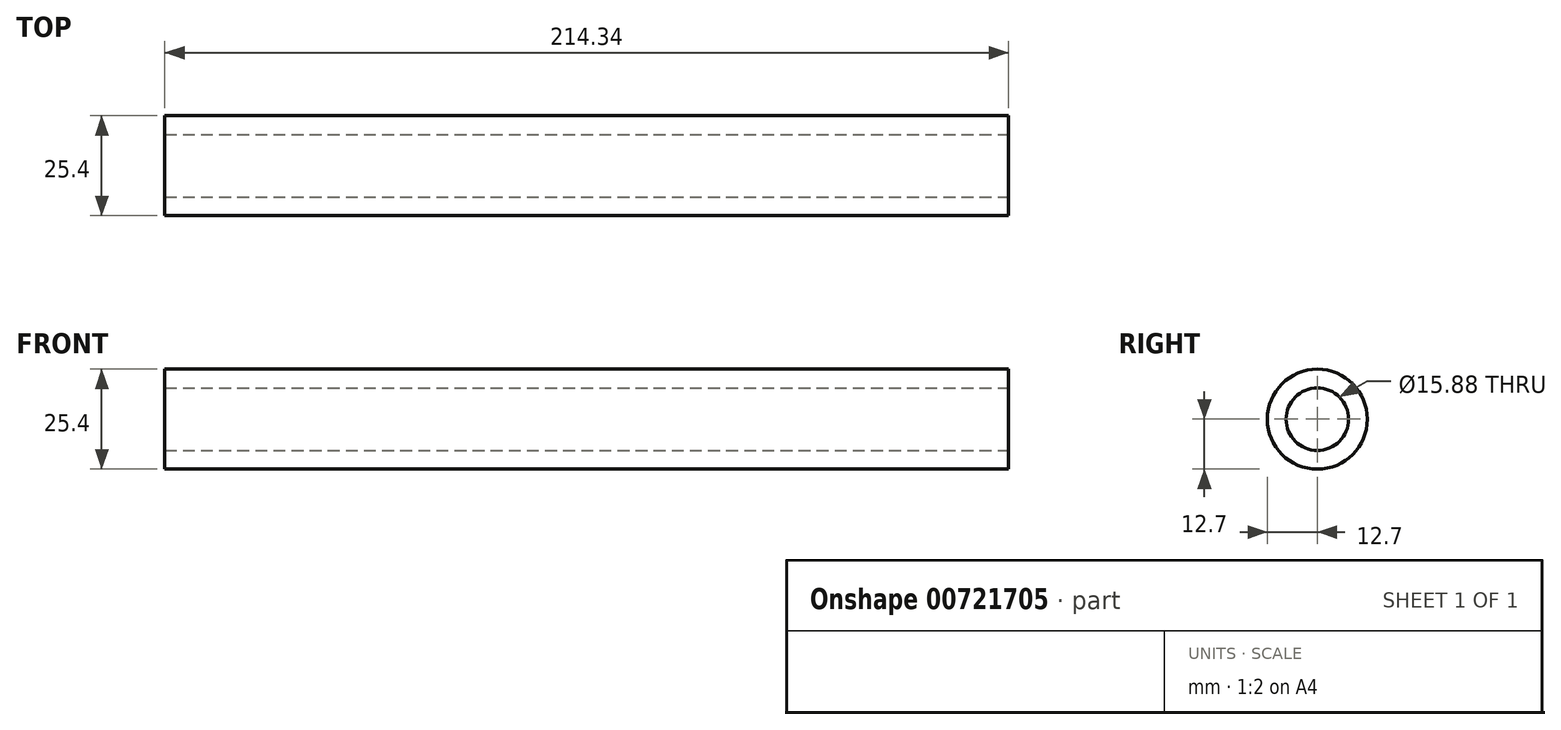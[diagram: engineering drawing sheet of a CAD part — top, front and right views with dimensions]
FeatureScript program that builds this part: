
annotation { "Feature Type Name" : "Feature", "Feature Type Description" : "" }
export const myFeature = defineFeature(function(context is Context, id is Id, definition is map)
    precondition{}
    {
        {
            var Q0;
            Q0=qCreatedBy(makeId("Front.planeOp"),FACE);
            var sketch = newSketch(context, id + "F0", { "sketchPlane" : qUnion([Q0])});
            skPoint(sketch, "E0.visualSharp", {"position": v(4518.56, 0) * mm});
            skPoint(sketch, "E1.orphan", {"position": v(-4518.56, 0) * mm});
            skLineSegment(sketch, "E2", {"start": v(0, 0) * mm, "end": v(214.34, 0) * mm});
            skSolve(sketch);
        }
        {
            var Q0;
            Q0=qCreatedBy(makeId("Right.planeOp"),FACE);
            var sketch = newSketch(context, id + "F1", { "sketchPlane" : qUnion([Q0])});
            skCircle(sketch, "E3", {"center": v(0, 0) * mm, "radius": 12.7 * mm});
            skCircle(sketch, "E4", {"center": v(0, 0) * mm, "radius": 7.94 * mm});
            skSolve(sketch);
        }
        {
            var Q0;
            Q0=qSketchRegion(id+"F1",true);
            var Q1;
            Q1=qConstructionFilter(qBodyType(qCreatedBy(id+"F0",EDGE),BodyType.WIRE),ConstructionObject.NO);
            sweep(context, id + "F2", {"profiles" : qUnion([Q0]), "path" : qUnion([Q1])});
        }
    });
